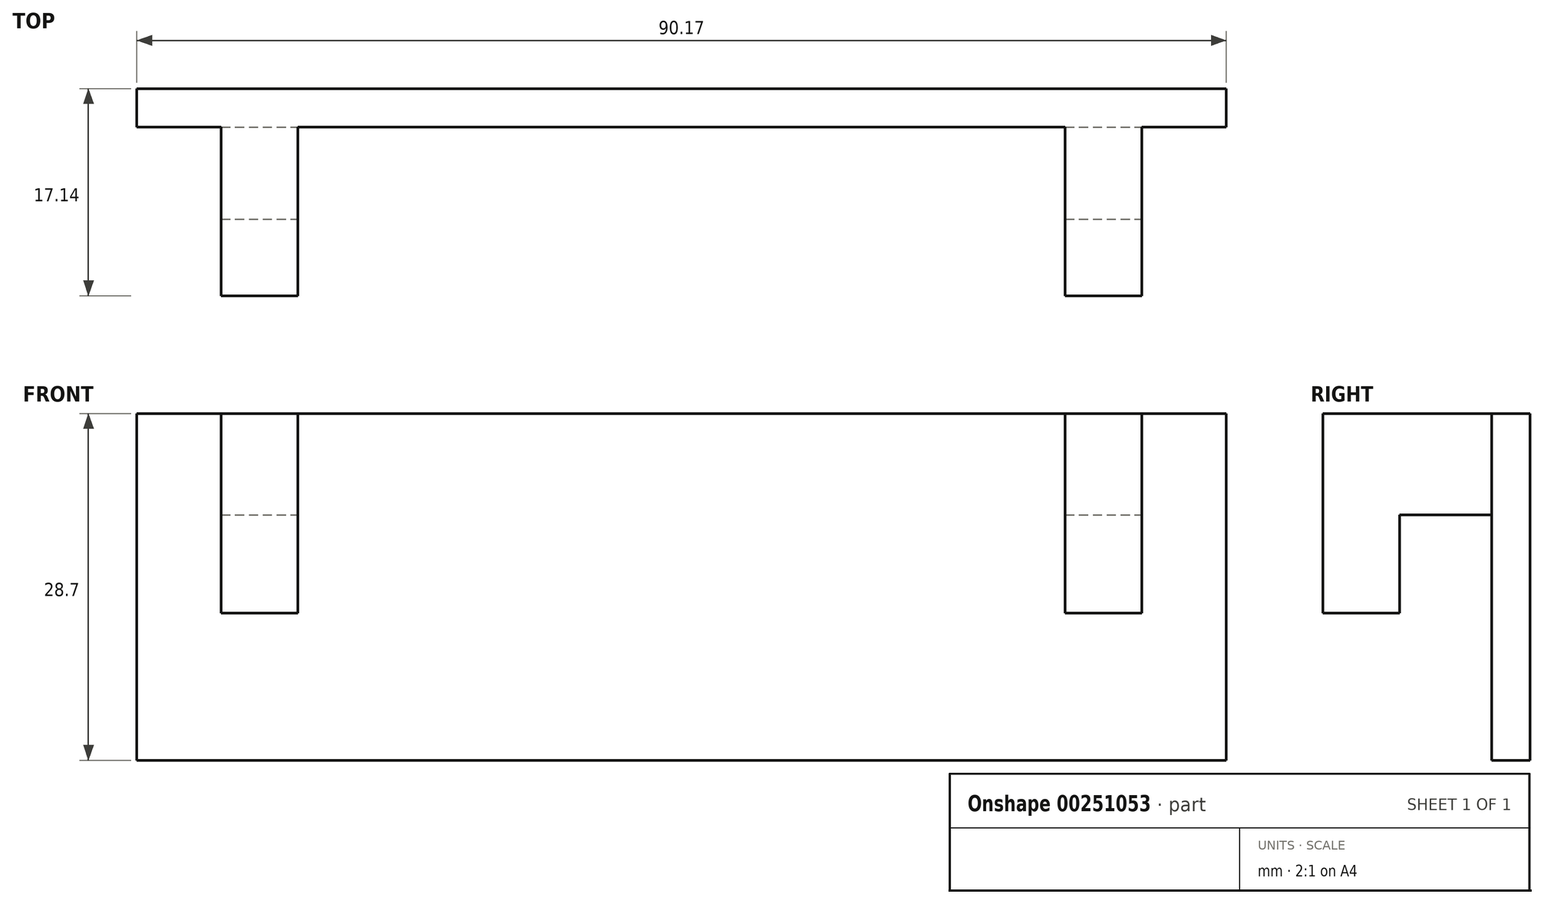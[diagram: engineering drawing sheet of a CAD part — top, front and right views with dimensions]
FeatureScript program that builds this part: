
annotation { "Feature Type Name" : "Feature", "Feature Type Description" : "" }
export const myFeature = defineFeature(function(context is Context, id is Id, definition is map)
    precondition{}
    {
        {
            var Q0;
            Q0=qCreatedBy(makeId("Front.planeOp"),FACE);
            var sketch = newSketch(context, id + "F0", { "sketchPlane" : qUnion([Q0])});
            skLineSegment(sketch, "E0.bottom", {"start": v(-60.68, 18.68) * mm, "end": v(29.49, 18.68) * mm});
            skLineSegment(sketch, "E0.top", {"start": v(-60.68, -10.02) * mm, "end": v(29.49, -10.02) * mm});
            skLineSegment(sketch, "E0.left", {"start": v(-60.68, 18.68) * mm, "end": v(-60.68, -10.02) * mm});
            skLineSegment(sketch, "E0.right", {"start": v(29.49, 18.68) * mm, "end": v(29.49, -10.02) * mm});
            skSolve(sketch);
        }
        {
            var Q0;
            Q0 = qSketchRegion(id + "F0", true);
            extrude(context, id + "F1", {"entities" : qUnion([Q0]), "depth" : 3.17 * mm});
        }
        {
            var Q0;
            Q0=makeQuery(id+"F1.opExtrude","CAP_FACE",FACE,{"disambiguationData":[OSD([sQuery(id+"F0.wireOp",EDGE,"E0.bottom"),sQuery(id+"F0.wireOp",EDGE,"E0.top"),sQuery(id+"F0.wireOp",EDGE,"E0.left"),sQuery(id+"F0.wireOp",EDGE,"E0.right")])],"isStart":false});
            var sketch = newSketch(context, id + "F2", { "sketchPlane" : qUnion([Q0])});
            skLineSegment(sketch, "E1.bottom", {"start": v(-53.7, 18.68) * mm, "end": v(-47.35, 18.68) * mm});
            skLineSegment(sketch, "E1.top", {"start": v(-53.7, 10.3) * mm, "end": v(-47.35, 10.3) * mm});
            skLineSegment(sketch, "E1.left", {"start": v(-53.7, 18.68) * mm, "end": v(-53.7, 10.3) * mm});
            skLineSegment(sketch, "E1.right", {"start": v(-47.35, 18.68) * mm, "end": v(-47.35, 10.3) * mm});
            skLineSegment(sketch, "E2.bottom", {"start": v(16.15, 18.68) * mm, "end": v(22.5, 18.68) * mm});
            skLineSegment(sketch, "E2.top", {"start": v(16.15, 10.3) * mm, "end": v(22.5, 10.3) * mm});
            skLineSegment(sketch, "E2.left", {"start": v(16.15, 18.68) * mm, "end": v(16.15, 10.3) * mm});
            skLineSegment(sketch, "E2.right", {"start": v(22.5, 18.68) * mm, "end": v(22.5, 10.3) * mm});
            skSolve(sketch);
        }
        {
            var Q0;
            Q0=makeQuery(id+"F2.imprint","IMPRINT",FACE,{"disambiguationData":[TD([[makeQuery(id+"F2.imprint","IMPRINT",EDGE,{"derivedFrom":sQuery(id+"F2.wireOp",EDGE,"E1.bottom")}),-1.0]])]});
            var Q1;
            Q1=makeQuery(id+"F2.imprint","IMPRINT",FACE,{"disambiguationData":[TD([[makeQuery(id+"F2.imprint","IMPRINT",EDGE,{"derivedFrom":sQuery(id+"F2.wireOp",EDGE,"E2.bottom")}),-1.0]])]});
            extrude(context, id + "F3", {"entities" : qUnion([Q0, Q1]), "operationType" : NewBodyOperationType.ADD, "depth" : 7.62 * mm});
        }
        {
            var Q0;
            Q0=makeQuery(id+"F3.boolean.opBoolean","MERGE",FACE,{"derivedFrom":[makeQuery(id+"F1.opExtrude","SWEPT_FACE",FACE,{"disambiguationData":[OSD([sQuery(id+"F0.wireOp",EDGE,"E0.bottom")])]}),makeQuery(id+"F3.opExtrude","SWEPT_FACE",FACE,{"disambiguationData":[OSD([sQuery(id+"F2.wireOp",EDGE,"E1.bottom")])]}),makeQuery(id+"F3.opExtrude","SWEPT_FACE",FACE,{"disambiguationData":[OSD([sQuery(id+"F2.wireOp",EDGE,"E2.bottom")])]})]});
            var sketch = newSketch(context, id + "F4", { "sketchPlane" : qUnion([Q0])});
            skLineSegment(sketch, "E3.bottom", {"start": v(-53.7, -10.8) * mm, "end": v(-47.35, -10.8) * mm});
            skLineSegment(sketch, "E3.top", {"start": v(-53.7, -17.14) * mm, "end": v(-47.35, -17.14) * mm});
            skLineSegment(sketch, "E3.left", {"start": v(-53.7, -10.8) * mm, "end": v(-53.7, -17.14) * mm});
            skLineSegment(sketch, "E3.right", {"start": v(-47.35, -10.8) * mm, "end": v(-47.35, -17.14) * mm});
            skLineSegment(sketch, "E4.bottom", {"start": v(16.15, -10.8) * mm, "end": v(22.5, -10.8) * mm});
            skLineSegment(sketch, "E4.top", {"start": v(16.15, -17.14) * mm, "end": v(22.5, -17.14) * mm});
            skLineSegment(sketch, "E4.left", {"start": v(16.15, -10.8) * mm, "end": v(16.15, -17.14) * mm});
            skLineSegment(sketch, "E4.right", {"start": v(22.5, -10.8) * mm, "end": v(22.5, -17.14) * mm});
            skSolve(sketch);
        }
        {
            var Q0;
            Q0 = qSketchRegion(id + "F4", true);
            extrude(context, id + "F5", {"entities" : qUnion([Q0]), "operationType" : NewBodyOperationType.ADD, "oppositeDirection" : true, "depth" : 16.5 * mm});
        }
    });
